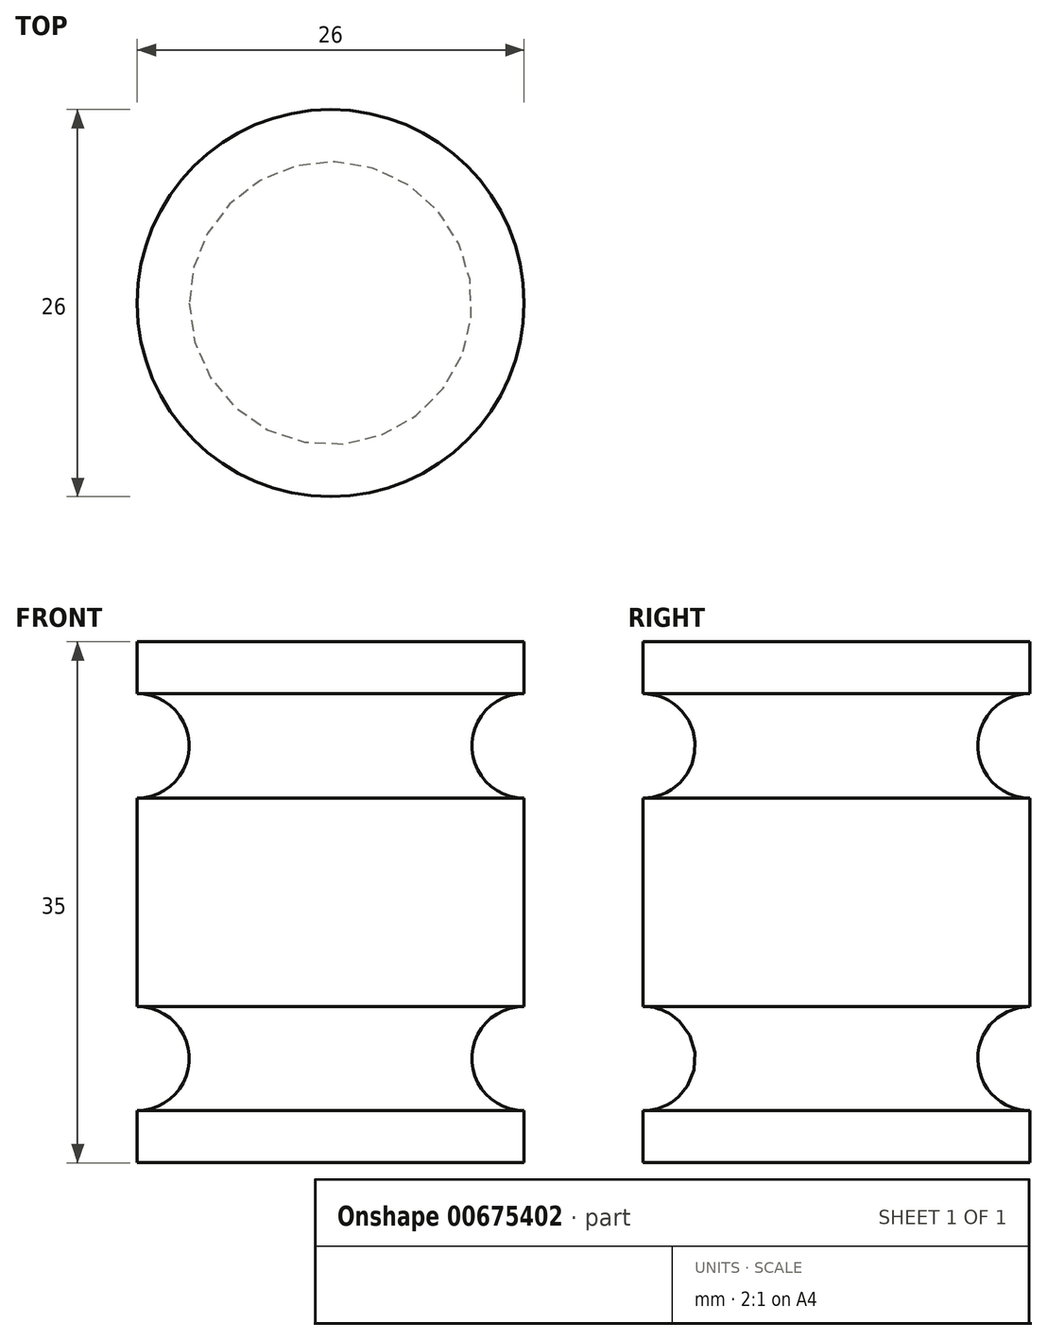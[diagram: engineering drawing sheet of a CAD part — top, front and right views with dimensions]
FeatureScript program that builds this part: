
annotation { "Feature Type Name" : "Feature", "Feature Type Description" : "" }
export const myFeature = defineFeature(function(context is Context, id is Id, definition is map)
    precondition{}
    {
        {
            var Q0;
            Q0=qCreatedBy(makeId("Front.planeOp"),FACE);
            var sketch = newSketch(context, id + "F0", { "sketchPlane" : qUnion([Q0])});
            skLineSegment(sketch, "E0", {"start": v(-44.36, -34.39) * mm, "end": v(-31.36, -34.39) * mm});
            skLineSegment(sketch, "E1", {"start": v(-31.36, -34.39) * mm, "end": v(-31.36, -30.89) * mm});
            skPoint(sketch, "E2.start.orphan", {"position": v(-44.36, 0) * mm});
            skLineSegment(sketch, "E3", {"start": v(-44.36, -34.39) * mm, "end": v(-44.36, 0.61) * mm});
            skLineSegment(sketch, "E4", {"start": v(-44.36, 0.61) * mm, "end": v(-31.36, 0.61) * mm});
            skArc(sketch, "E5", {"start": v(-31.36, -23.89) * mm, "mid": v(-34.86, -27.39) * mm, "end": v(-31.36, -30.89) * mm});
            skArc(sketch, "E6", {"start": v(-31.36, -2.89) * mm, "mid": v(-34.86, -6.39) * mm, "end": v(-31.36, -9.89) * mm});
            skLineSegment(sketch, "E7.trimOffspring", {"start": v(-31.36, -2.89) * mm, "end": v(-31.36, 0.61) * mm});
            skLineSegment(sketch, "E8.trimOffspring", {"start": v(-31.36, -23.89) * mm, "end": v(-31.36, -9.89) * mm});
            skSolve(sketch);
        }
        {
            var Q0;
            Q0=makeQuery(id+"F0.imprint","IMPRINT",FACE,{"disambiguationData":[TD([[makeQuery(id+"F0.imprint","IMPRINT",EDGE,{"derivedFrom":sQuery(id+"F0.wireOp",EDGE,"E0")}),1.0]])]});
            var Q1;
            Q1=sQuery(id+"F0.wireOp",EDGE,"E3");
            revolve(context, id + "F1", {"entities" : qUnion([Q0]), "axis" : qUnion([Q1]), "revolveType" : RevolveType.FULL});
        }
    });
